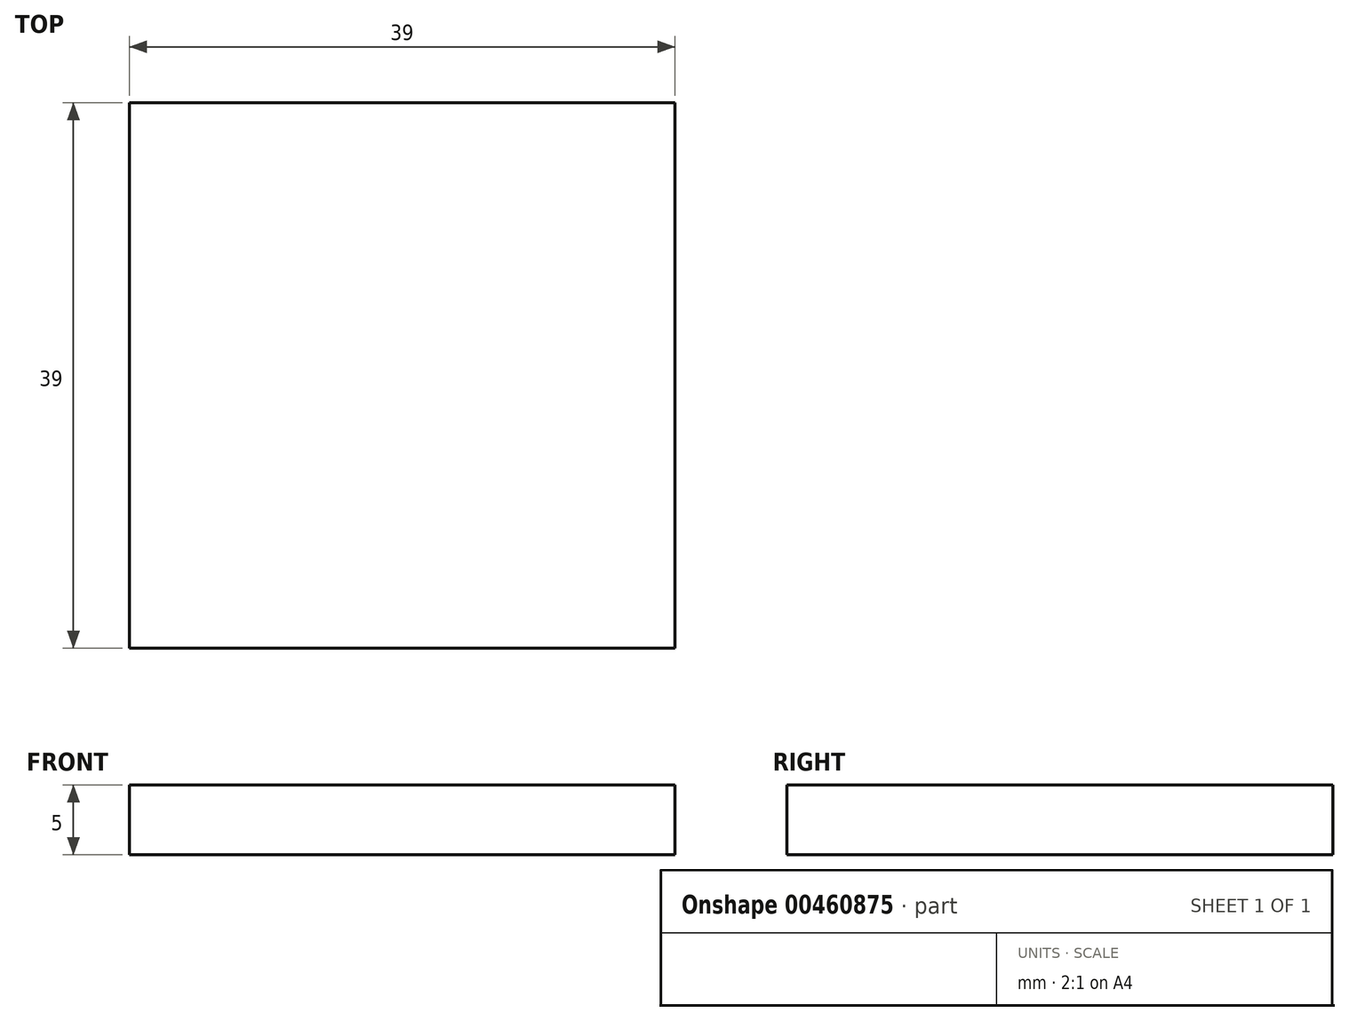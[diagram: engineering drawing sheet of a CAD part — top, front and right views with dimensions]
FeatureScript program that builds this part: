
annotation { "Feature Type Name" : "Feature", "Feature Type Description" : "" }
export const myFeature = defineFeature(function(context is Context, id is Id, definition is map)
    precondition{}
    {
        {
            var Q0;
            Q0=qCreatedBy(makeId("Top.planeOp"),FACE);
            var sketch = newSketch(context, id + "F0", { "sketchPlane" : qUnion([Q0])});
            skLineSegment(sketch, "E0.bottom", {"start": v(19.5, 19.5) * mm, "end": v(-19.5, 19.5) * mm});
            skLineSegment(sketch, "E0.top", {"start": v(19.5, -19.5) * mm, "end": v(-19.5, -19.5) * mm});
            skLineSegment(sketch, "E0.left", {"start": v(19.5, 19.5) * mm, "end": v(19.5, -19.5) * mm});
            skLineSegment(sketch, "E0.right", {"start": v(-19.5, 19.5) * mm, "end": v(-19.5, -19.5) * mm});
            skPoint(sketch, "E0.middle", {"position": v(0, 0) * mm});
            skSolve(sketch);
        }
        {
            var Q0;
            Q0=qSketchRegion(id+"F0",true);
            extrude(context, id + "F1", {"entities" : qUnion([Q0]), "depth" : 5 * mm});
        }
    });
